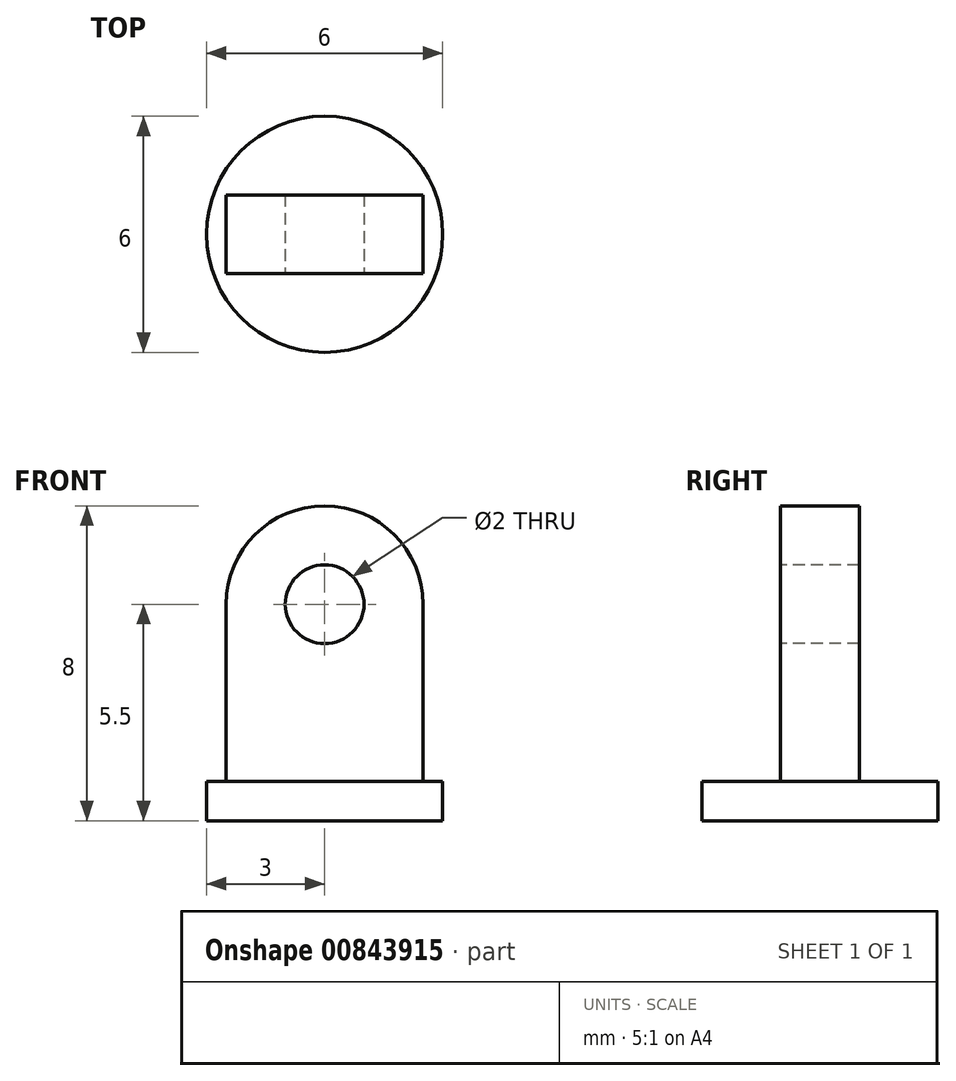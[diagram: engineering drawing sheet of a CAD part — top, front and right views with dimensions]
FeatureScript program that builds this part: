
annotation { "Feature Type Name" : "Feature", "Feature Type Description" : "" }
export const myFeature = defineFeature(function(context is Context, id is Id, definition is map)
    precondition{}
    {
        {
            var Q0;
            Q0=qCreatedBy(makeId("Top.planeOp"),FACE);
            var sketch = newSketch(context, id + "F0", { "sketchPlane" : qUnion([Q0])});
            skCircle(sketch, "E0", {"center": v(0, 0) * mm, "radius": 3 * mm});
            skSolve(sketch);
        }
        {
            var Q0;
            Q0 = qSketchRegion(id + "F0", true);
            extrude(context, id + "F1", {"entities" : qUnion([Q0]), "depth" : 1 * mm, "offsetDistance" : 25 * mm});
        }
        {
            var Q0;
            Q0=makeQuery(id+"F1.opExtrude","CAP_FACE",FACE,{"disambiguationData":[OSD([sQuery(id+"F0.wireOp",EDGE,"E0")])],"isStart":false});
            var sketch = newSketch(context, id + "F2", { "sketchPlane" : qUnion([Q0])});
            skLineSegment(sketch, "E1.bottom", {"start": v(2.5, 1) * mm, "end": v(-2.5, 1) * mm});
            skLineSegment(sketch, "E1.top", {"start": v(2.5, -1) * mm, "end": v(-2.5, -1) * mm});
            skLineSegment(sketch, "E1.left", {"start": v(2.5, 1) * mm, "end": v(2.5, -1) * mm});
            skLineSegment(sketch, "E1.right", {"start": v(-2.5, 1) * mm, "end": v(-2.5, -1) * mm});
            skPoint(sketch, "E1.middle", {"position": v(0, 0) * mm});
            skSolve(sketch);
        }
        {
            var Q0;
            Q0 = qSketchRegion(id + "F2", true);
            extrude(context, id + "F3", {"entities" : qUnion([Q0]), "operationType" : NewBodyOperationType.ADD, "depth" : 4.5 * mm, "offsetDistance" : 25 * mm});
        }
        {
            var Q0;
            Q0=qCreatedBy(makeId("Front.planeOp"),FACE);
            var sketch = newSketch(context, id + "F4", { "sketchPlane" : qUnion([Q0])});
            skArc(sketch, "E2", {"start": v(2.5, 5.5) * mm, "mid": v(0, 8) * mm, "end": v(-2.5, 5.5) * mm});
            skLineSegment(sketch, "E3", {"start": v(0, 5.5) * mm, "end": v(-2.5, 5.5) * mm});
            skLineSegment(sketch, "E4", {"start": v(0, 5.5) * mm, "end": v(2.5, 5.5) * mm});
            skSolve(sketch);
        }
        {
            var Q0;
            Q0=makeQuery(id+"F4.imprint","IMPRINT",FACE,{"disambiguationData":[TD([[makeQuery(id+"F4.imprint","IMPRINT",EDGE,{"derivedFrom":sQuery(id+"F4.wireOp",EDGE,"E2")}),1.0]])]});
            extrude(context, id + "F5", {"entities" : qUnion([Q0]), "operationType" : NewBodyOperationType.ADD, "endBound" : BoundingType.SYMMETRIC, "depth" : 2 * mm, "offsetDistance" : 25 * mm});
        }
        {
            var Q0;
            Q0=makeQuery(id+"F5.boolean.opBoolean","MERGE",FACE,{"derivedFrom":[makeQuery(id+"F3.opExtrude","SWEPT_FACE",FACE,{"disambiguationData":[OSD([sQuery(id+"F2.wireOp",EDGE,"E1.top")])]}),makeQuery(id+"F5.opExtrude","CAP_FACE",FACE,{"disambiguationData":[OSD([sQuery(id+"F4.wireOp",EDGE,"E2"),sQuery(id+"F4.wireOp",EDGE,"E3"),sQuery(id+"F4.wireOp",EDGE,"E4")])],"isStart":false})]});
            var sketch = newSketch(context, id + "F6", { "sketchPlane" : qUnion([Q0])});
            skCircle(sketch, "E5", {"center": v(0, 5.5) * mm, "radius": 1 * mm});
            skSolve(sketch);
        }
        {
            var Q0;
            Q0 = qSketchRegion(id + "F6", true);
            extrude(context, id + "F7", {"entities" : qUnion([Q0]), "operationType" : NewBodyOperationType.REMOVE, "oppositeDirection" : true, "depth" : 25 * mm, "offsetDistance" : 25 * mm});
        }
    });
